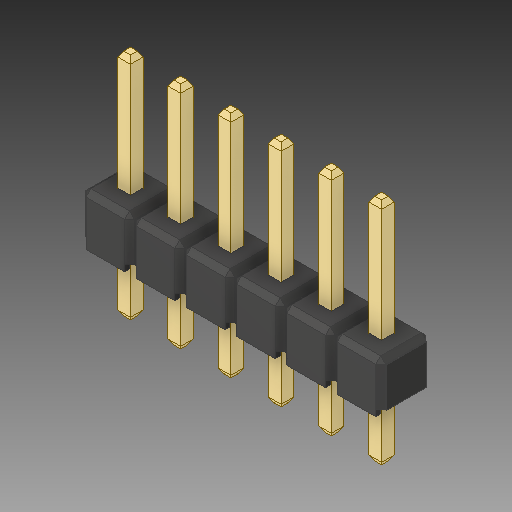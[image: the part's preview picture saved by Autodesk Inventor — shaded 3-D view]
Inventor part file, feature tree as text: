
AUTODESK INVENTOR PART (.ipt)
format: ipt  version: 2019 (Build 230136000, 136)  size: 277,504 bytes
history: native  units: in
note: dims shown in document units (in); Inventor stores cm internally (conversion verified against a paired STEP export)
features: other x11, chamfer x1
ambient origin geometry x8: Origin, YZ Plane, XZ Plane, XY Plane, X Axis, Y Axis, Z Axis, Center Point
bodies: Solid1 (feature_tree), Solid2 (feature_tree), Solid3 (feature_tree), Solid4 (feature_tree), Solid5 (feature_tree), Solid6 (feature_tree), Solid7 (feature_tree), Solid8 (feature_tree), Solid9 (feature_tree), Solid10 (feature_tree), Solid11 (feature_tree), Solid12 (feature_tree)
feature tree (12):
  chamfer  "Chamfer2"  [1 undecoded]
  other  "Boss-Extrude3"
  other  "LPattern1[1]"
  other  "LPattern1[2]"
  other  "LPattern1[3]"
  other  "LPattern1[4]"
  other  "LPattern1[5]"
  other  "LPattern1[6]"
  other  "LPattern1[7]"
  other  "LPattern1[8]"
  other  "LPattern1[9]"
  other  "LPattern1[10]"
note: 1 required parameter value undecoded (feature->parameter linkage not recoverable at this tier; creation-order binding heuristic only, values carry confidence <= 0.55)
